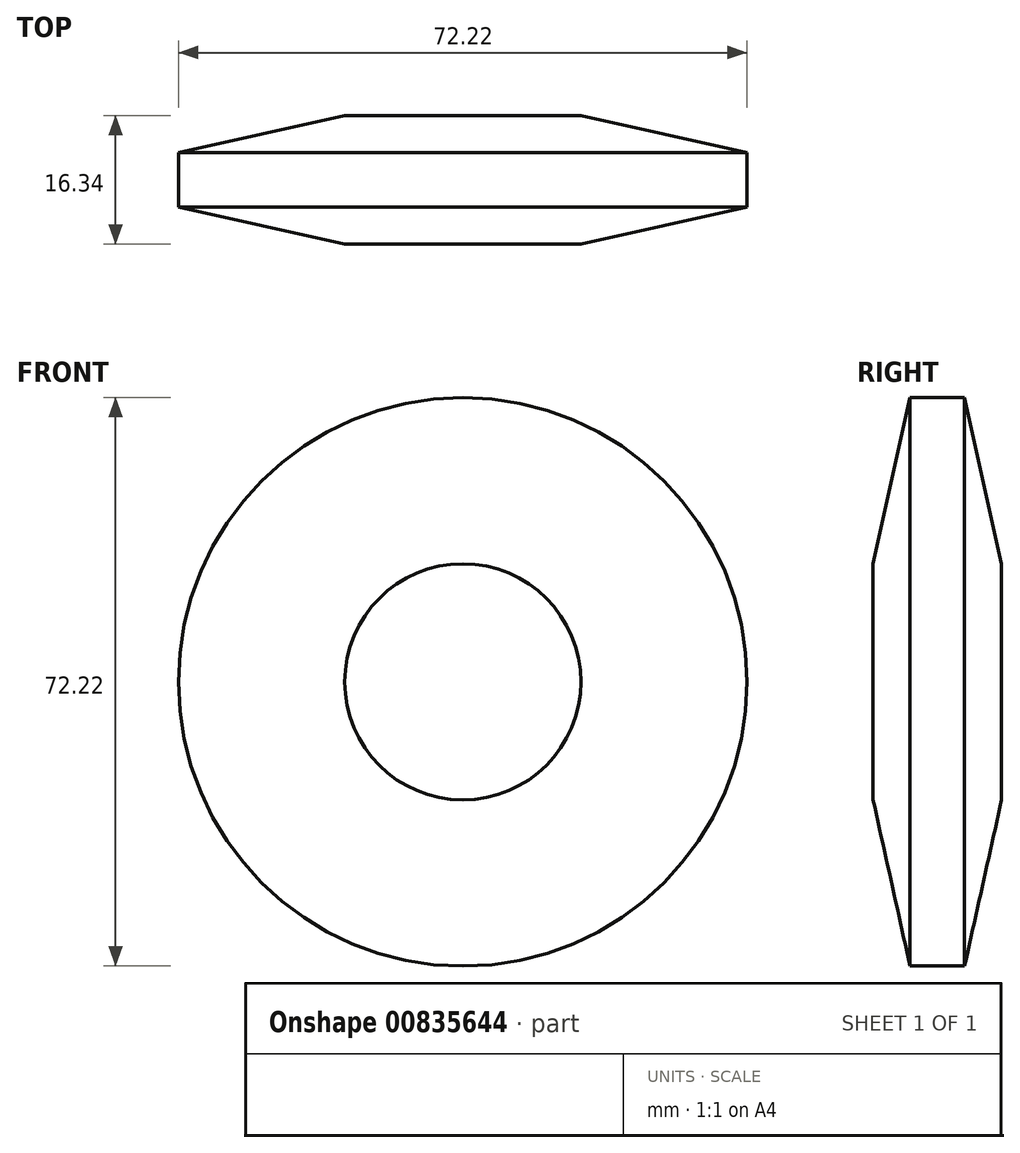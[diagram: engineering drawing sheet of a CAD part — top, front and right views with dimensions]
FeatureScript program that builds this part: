
annotation { "Feature Type Name" : "Feature", "Feature Type Description" : "" }
export const myFeature = defineFeature(function(context is Context, id is Id, definition is map)
    precondition{}
    {
        {
            var Q0;
            Q0=qCreatedBy(makeId("Right.planeOp"),FACE);
            var sketch = newSketch(context, id + "F0", { "sketchPlane" : qUnion([Q0])});
            skLineSegment(sketch, "E0", {"start": v(0, 36.11) * mm, "end": v(3.46, 36.11) * mm});
            skLineSegment(sketch, "E1", {"start": v(3.46, 36.11) * mm, "end": v(8.17, 15) * mm});
            skLineSegment(sketch, "E2", {"start": v(8.17, 15) * mm, "end": v(8.17, 0) * mm});
            skLineSegment(sketch, "E3", {"start": v(0, 0) * mm, "end": v(8.17, 0) * mm});
            skLineSegment(sketch, "E4.MirrorCS", {"start": v(0, 36.11) * mm, "end": v(-3.46, 36.11) * mm});
            skLineSegment(sketch, "E5.MirrorCS", {"start": v(-8.17, 15) * mm, "end": v(-8.17, 0) * mm});
            skLineSegment(sketch, "E6.MirrorCS", {"start": v(0, 0) * mm, "end": v(-8.17, 0) * mm});
            skLineSegment(sketch, "E7.MirrorCS", {"start": v(-3.46, 36.11) * mm, "end": v(-8.17, 15) * mm});
            skSolve(sketch);
        }
        {
            var Q0;
            Q0=makeQuery(id+"F0.imprint","IMPRINT",FACE,{"disambiguationData":[TD([[makeQuery(id+"F0.imprint","IMPRINT",EDGE,{"derivedFrom":sQuery(id+"F0.wireOp",EDGE,"E0")}),-1.0]])]});
            var Q1;
            Q1=sQuery(id+"F0.wireOp",EDGE,"E3");
            revolve(context, id + "F1", {"surfaceOperationType" : NewSurfaceOperationType.NEW, "entities" : qUnion([Q0]), "axis" : qUnion([Q1]), "revolveType" : RevolveType.FULL});
        }
    });
